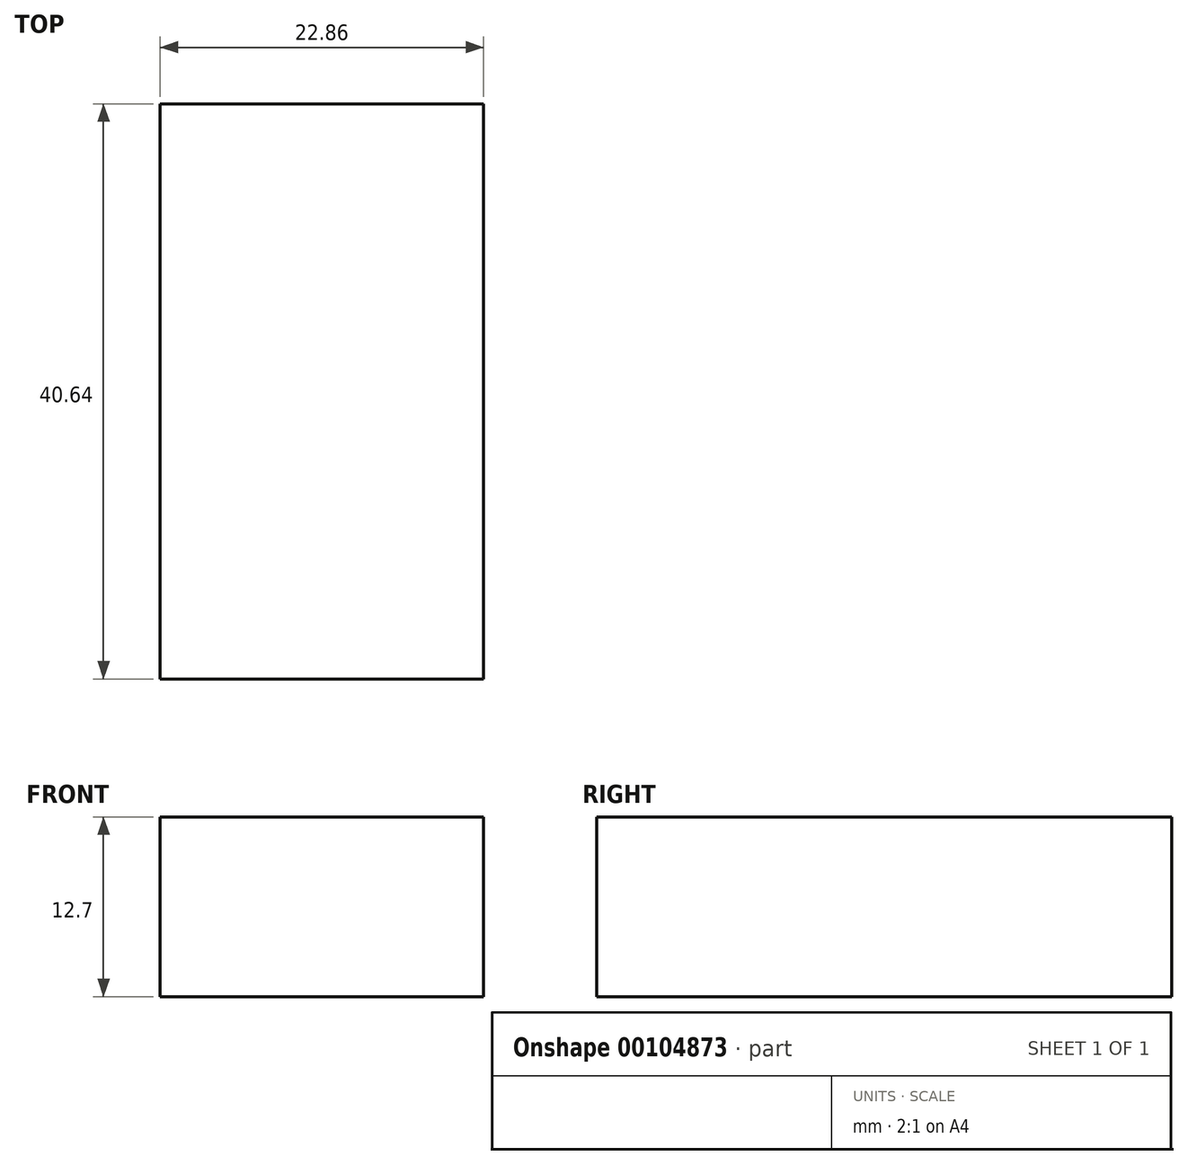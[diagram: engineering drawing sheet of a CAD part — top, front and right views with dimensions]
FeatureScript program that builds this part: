
annotation { "Feature Type Name" : "Feature", "Feature Type Description" : "" }
export const myFeature = defineFeature(function(context is Context, id is Id, definition is map)
    precondition{}
    {
        {
            var Q0;
            Q0=qCreatedBy(makeId("Top.planeOp"),FACE);
            var sketch = newSketch(context, id + "F0", { "sketchPlane" : qUnion([Q0])});
            skLineSegment(sketch, "E0.bottom", {"start": v(-11.43, 20.32) * mm, "end": v(11.43, 20.32) * mm});
            skLineSegment(sketch, "E0.top", {"start": v(-11.43, -20.32) * mm, "end": v(11.43, -20.32) * mm});
            skLineSegment(sketch, "E0.left", {"start": v(-11.43, 20.32) * mm, "end": v(-11.43, -20.32) * mm});
            skLineSegment(sketch, "E0.right", {"start": v(11.43, 20.32) * mm, "end": v(11.43, -20.32) * mm});
            skPoint(sketch, "E0.middle", {"position": v(0, 0) * mm});
            skSolve(sketch);
        }
        {
            var Q0;
            Q0=makeQuery(id+"F0.imprint","IMPRINT",FACE,{"disambiguationData":[TD([[makeQuery(id+"F0.imprint","IMPRINT",EDGE,{"derivedFrom":sQuery(id+"F0.wireOp",EDGE,"E0.bottom")}),-1.0]])]});
            extrude(context, id + "F1", {"entities" : qUnion([Q0]), "depth" : 12.7 * mm});
        }
    });
